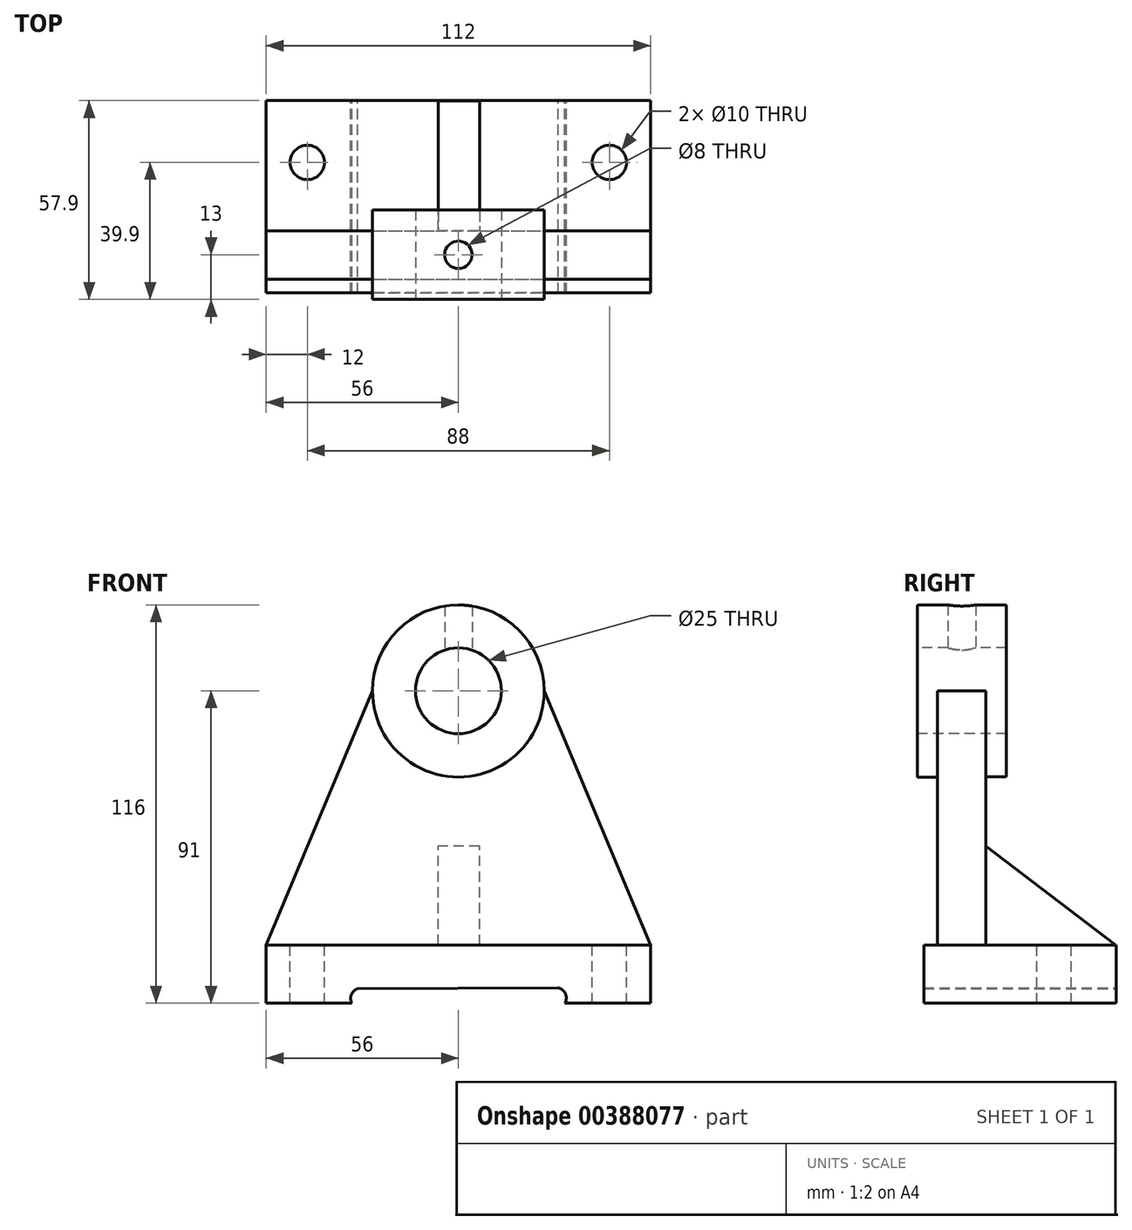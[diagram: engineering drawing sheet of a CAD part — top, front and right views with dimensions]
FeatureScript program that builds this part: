
annotation { "Feature Type Name" : "Feature", "Feature Type Description" : "" }
export const myFeature = defineFeature(function(context is Context, id is Id, definition is map)
    precondition{}
    {
        {
            var Q0;
            Q0=qCreatedBy(makeId("Front.planeOp"),FACE);
            var sketch = newSketch(context, id + "F0", { "sketchPlane" : qUnion([Q0])});
            skCircle(sketch, "E0", {"center": v(0, 0) * mm, "radius": 25 * mm});
            skSolve(sketch);
        }
        {
            var Q0;
            Q0 = qSketchRegion(id + "F0", true);
            extrude(context, id + "F1", {"entities" : qUnion([Q0]), "depth" : 26 * mm});
        }
        {
            var Q0;
            Q0=makeQuery(id+"F1.opExtrude","CAP_FACE",FACE,{"disambiguationData":[OSD([sQuery(id+"F0.wireOp",EDGE,"E0")])],"isStart":false});
            var sketch = newSketch(context, id + "F2", { "sketchPlane" : qUnion([Q0])});
            skLineSegment(sketch, "E1", {"start": v(-56, -74) * mm, "end": v(56, -74) * mm});
            skLineSegment(sketch, "E2", {"start": v(56, -74) * mm, "end": v(25, 0) * mm});
            skLineSegment(sketch, "E3", {"start": v(-56, -74) * mm, "end": v(-25, 0) * mm});
            skLineSegment(sketch, "E4", {"start": v(-25, 0) * mm, "end": v(25, 0) * mm});
            skSolve(sketch);
        }
        {
            var Q0;
            Q0 = qSketchRegion(id + "F2", true);
            extrude(context, id + "F3", {"entities" : qUnion([Q0]), "operationType" : NewBodyOperationType.ADD, "oppositeDirection" : true, "depth" : 20 * mm});
        }
        {
            var Q0;
            Q0=makeQuery(id+"F3.boolean.opBoolean","MERGE",FACE,{"derivedFrom":[makeQuery(id+"F1.opExtrude","CAP_FACE",FACE,{"disambiguationData":[OSD([sQuery(id+"F0.wireOp",EDGE,"E0")])],"isStart":false}),makeQuery(id+"F3.opExtrude","CAP_FACE",FACE,{"disambiguationData":[OSD([sQuery(id+"F2.wireOp",EDGE,"E1"),sQuery(id+"F2.wireOp",EDGE,"E2"),sQuery(id+"F2.wireOp",EDGE,"E3"),sQuery(id+"F2.wireOp",EDGE,"E4")])],"isStart":true})]});
            var sketch = newSketch(context, id + "F4", { "sketchPlane" : qUnion([Q0])});
            skLineSegment(sketch, "E5", {"start": v(-25, 0) * mm, "end": v(-56, -74) * mm});
            skLineSegment(sketch, "E6", {"start": v(-56, -74) * mm, "end": v(56, -74) * mm});
            skArc(sketch, "E7", {"start": v(-25, 0) * mm, "mid": v(0, -25.12) * mm, "end": v(25, 0) * mm});
            skLineSegment(sketch, "E8", {"start": v(25, 0) * mm, "end": v(56, -74) * mm});
            skSolve(sketch);
        }
        {
            var Q0;
            Q0 = qSketchRegion(id + "F4", true);
            extrude(context, id + "F5", {"entities" : qUnion([Q0]), "operationType" : NewBodyOperationType.REMOVE, "oppositeDirection" : true, "depth" : 5.7 * mm});
        }
        {
            var Q0;
            Q0=makeQuery(id+"F3.boolean.opBoolean","MERGE",FACE,{"derivedFrom":[makeQuery(id+"F1.opExtrude","CAP_FACE",FACE,{"disambiguationData":[OSD([sQuery(id+"F0.wireOp",EDGE,"E0")])],"isStart":false}),makeQuery(id+"F3.opExtrude","CAP_FACE",FACE,{"disambiguationData":[OSD([sQuery(id+"F2.wireOp",EDGE,"E1"),sQuery(id+"F2.wireOp",EDGE,"E2"),sQuery(id+"F2.wireOp",EDGE,"E3"),sQuery(id+"F2.wireOp",EDGE,"E4")])],"isStart":true})]});
            var sketch = newSketch(context, id + "F6", { "sketchPlane" : qUnion([Q0])});
            skCircle(sketch, "E9", {"center": v(0, 0) * mm, "radius": 12.5 * mm});
            skSolve(sketch);
        }
        {
            var Q0;
            Q0 = qSketchRegion(id + "F4", true);
            extrude(context, id + "F7", {"entities" : qUnion([Q0]), "operationType" : NewBodyOperationType.REMOVE, "oppositeDirection" : true, "depth" : 5.9 * mm});
        }
        {
            var Q0;
            Q0 = qSketchRegion(id + "F6", true);
            extrude(context, id + "F8", {"entities" : qUnion([Q0]), "operationType" : NewBodyOperationType.REMOVE, "endBound" : BoundingType.THROUGH_ALL, "oppositeDirection" : true, "depth" : 25 * mm});
        }
        {
            var Q0;
            Q0=makeQuery(id+"F3.opExtrude","SWEPT_FACE",FACE,{"disambiguationData":[OSD([sQuery(id+"F2.wireOp",EDGE,"E1")])]});
            var sketch = newSketch(context, id + "F9", { "sketchPlane" : qUnion([Q0])});
            skPoint(sketch, "E10.firstSnap0", {"position": v(-56, 13.05) * mm});
            skLineSegment(sketch, "E10.bottom", {"start": v(-56, 24.1) * mm, "end": v(56, 24.1) * mm});
            skLineSegment(sketch, "E10.top", {"start": v(-56, -31.9) * mm, "end": v(56, -31.9) * mm});
            skLineSegment(sketch, "E10.left", {"start": v(-56, 24.1) * mm, "end": v(-56, -31.9) * mm});
            skLineSegment(sketch, "E10.right", {"start": v(56, 24.1) * mm, "end": v(56, -31.9) * mm});
            skSolve(sketch);
        }
        {
            var Q0;
            Q0 = qSketchRegion(id + "F9", true);
            extrude(context, id + "F10", {"entities" : qUnion([Q0]), "operationType" : NewBodyOperationType.ADD, "depth" : 17 * mm});
        }
        {
            var Q0;
            Q0=makeQuery(id+"F3.opExtrude","CAP_FACE",FACE,{"disambiguationData":[OSD([sQuery(id+"F2.wireOp",EDGE,"E1"),sQuery(id+"F2.wireOp",EDGE,"E2"),sQuery(id+"F2.wireOp",EDGE,"E3"),sQuery(id+"F2.wireOp",EDGE,"E4")])],"isStart":false});
            var sketch = newSketch(context, id + "F11", { "sketchPlane" : qUnion([Q0])});
            skLineSegment(sketch, "E11.bottom", {"start": v(-6.15, -74) * mm, "end": v(5.85, -74) * mm});
            skLineSegment(sketch, "E11.top", {"start": v(-6.15, -45.17) * mm, "end": v(5.85, -45.17) * mm});
            skLineSegment(sketch, "E11.left", {"start": v(-6.15, -74) * mm, "end": v(-6.15, -45.17) * mm});
            skLineSegment(sketch, "E11.right", {"start": v(5.85, -74) * mm, "end": v(5.85, -45.17) * mm});
            skSolve(sketch);
        }
        {
            var Q0;
            Q0 = qSketchRegion(id + "F11", true);
            extrude(context, id + "F12", {"entities" : qUnion([Q0]), "operationType" : NewBodyOperationType.ADD, "depth" : 37.8 * mm});
        }
        {
            var Q0;
            Q0=makeQuery(id+"F12.opExtrude","SWEPT_FACE",FACE,{"disambiguationData":[OSD([sQuery(id+"F11.wireOp",EDGE,"E11.right")])]});
            var sketch = newSketch(context, id + "F13", { "sketchPlane" : qUnion([Q0])});
            skLineSegment(sketch, "E12", {"start": v(6, -45.17) * mm, "end": v(-31.8, -74) * mm});
            skLineSegment(sketch, "E13", {"start": v(-31.8, -74) * mm, "end": v(-31.8, -45.17) * mm});
            skLineSegment(sketch, "E14", {"start": v(-31.8, -45.17) * mm, "end": v(6, -45.17) * mm});
            skSolve(sketch);
        }
        {
            var Q0;
            Q0 = qSketchRegion(id + "F13", true);
            extrude(context, id + "F14", {"entities" : qUnion([Q0]), "operationType" : NewBodyOperationType.REMOVE, "endBound" : BoundingType.THROUGH_ALL, "oppositeDirection" : true, "depth" : 25 * mm});
        }
        {
            var Q0;
            {var subQ1=sQuery(id+"F9.wireOp",EDGE,"E10.top");var subQ3=sQuery(id+"F9.wireOp",EDGE,"E10.left");var subQ4=sQuery(id+"F9.wireOp",EDGE,"E10.right");Q0=makeQuery(id+"F10.boolean.opBoolean","SPLIT",FACE,{"disambiguationData":[TD([makeQuery(id+"F10.opExtrude","SWEPT_FACE",FACE,{"disambiguationData":[OSD([subQ1])]})])],"derivedFrom":makeQuery(id+"F10.opExtrude","CAP_FACE",FACE,{"disambiguationData":[OSD([sQuery(id+"F9.wireOp",EDGE,"E10.bottom"),subQ1,subQ3,subQ4])],"isStart":true})});}
            var sketch = newSketch(context, id + "F15", { "sketchPlane" : qUnion([Q0])});
            skCircle(sketch, "E15", {"center": v(-44, 13.9) * mm, "radius": 5 * mm});
            skCircle(sketch, "E16", {"center": v(44, 13.9) * mm, "radius": 5 * mm});
            skSolve(sketch);
        }
        {
            var Q0;
            Q0 = qSketchRegion(id + "F15", true);
            extrude(context, id + "F16", {"entities" : qUnion([Q0]), "operationType" : NewBodyOperationType.REMOVE, "endBound" : BoundingType.THROUGH_ALL, "oppositeDirection" : true, "depth" : 25 * mm});
        }
        {
            var Q0;
            Q0=makeQuery(id+"F10.opExtrude","SWEPT_FACE",FACE,{"disambiguationData":[OSD([sQuery(id+"F9.wireOp",EDGE,"E10.top")])]});
            var sketch = newSketch(context, id + "F17", { "sketchPlane" : qUnion([Q0])});
            skArc(sketch, "E17", {"start": v(31, -91) * mm, "mid": v(31.15, -88.46) * mm, "end": v(29.3, -86.72) * mm});
            skArc(sketch, "E18", {"start": v(-29.08, -86.5) * mm, "mid": v(-31.2, -88.25) * mm, "end": v(-31, -91) * mm});
            skLineSegment(sketch, "E19", {"start": v(29.3, -86.72) * mm, "end": v(-29.08, -86.5) * mm});
            skLineSegment(sketch, "E20", {"start": v(-31, -91) * mm, "end": v(31, -91) * mm});
            skSolve(sketch);
        }
        {
            var Q0;
            Q0 = qSketchRegion(id + "F17", true);
            extrude(context, id + "F18", {"entities" : qUnion([Q0]), "operationType" : NewBodyOperationType.REMOVE, "endBound" : BoundingType.THROUGH_ALL, "oppositeDirection" : true, "depth" : 25 * mm});
        }
        {
            var Q0;
            Q0=qCreatedBy(makeId("Top.planeOp"),FACE);
            var sketch = newSketch(context, id + "F19", { "sketchPlane" : qUnion([Q0])});
            skCircle(sketch, "E21", {"center": v(0, -13) * mm, "radius": 4 * mm});
            skSolve(sketch);
        }
        {
            var Q0;
            Q0 = qSketchRegion(id + "F19", true);
            extrude(context, id + "F20", {"entities" : qUnion([Q0]), "operationType" : NewBodyOperationType.REMOVE, "endBound" : BoundingType.THROUGH_ALL, "depth" : 118 * mm});
        }
    });
